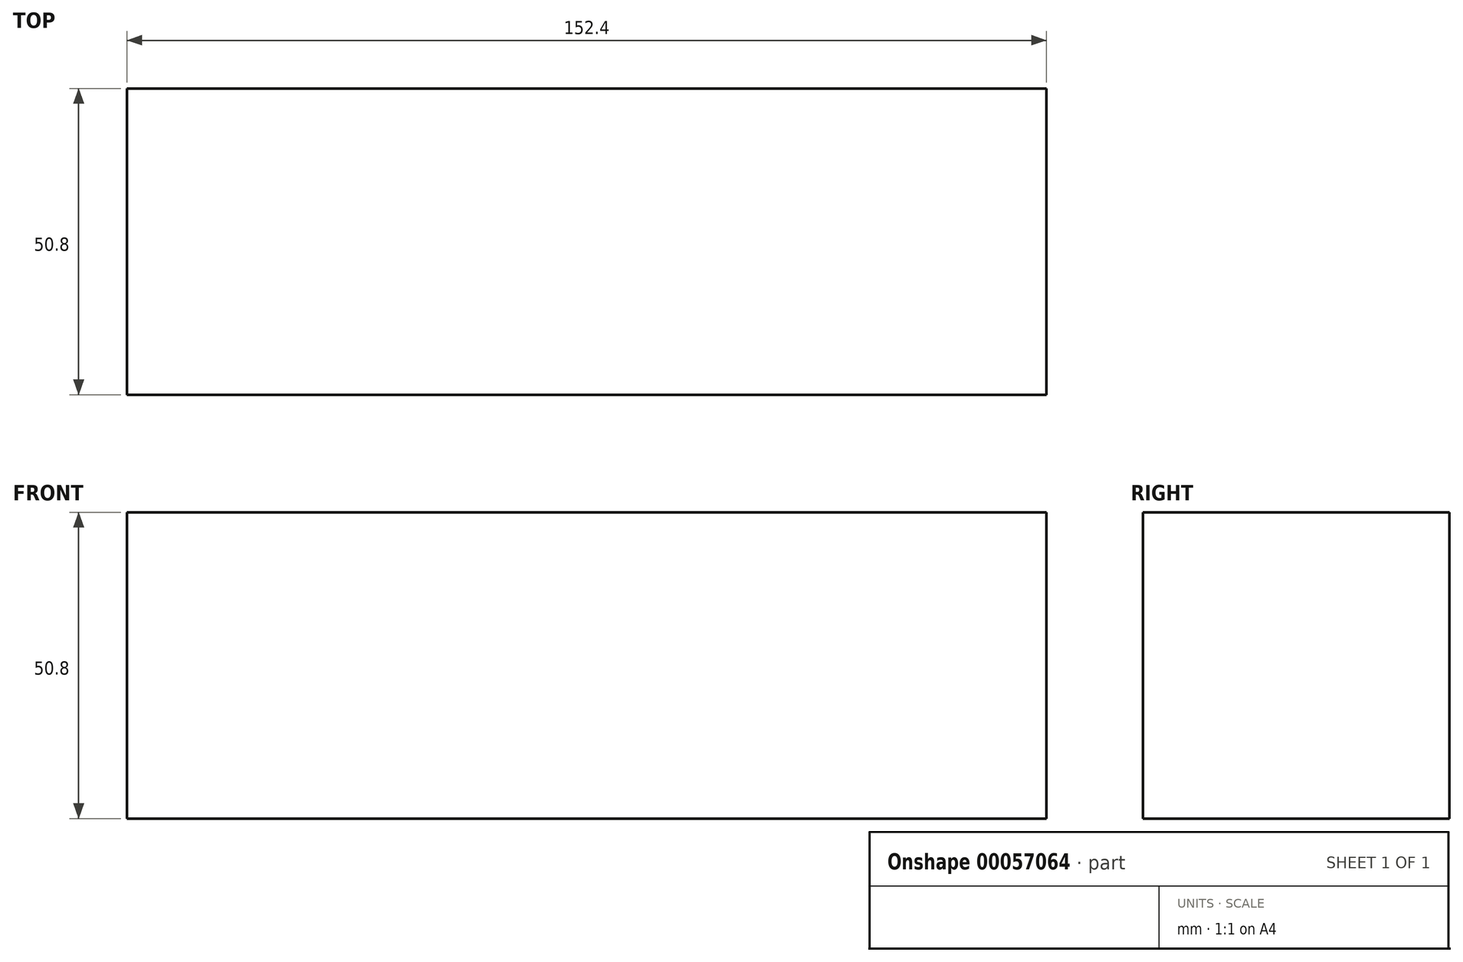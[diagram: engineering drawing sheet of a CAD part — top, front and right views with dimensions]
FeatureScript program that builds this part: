
annotation { "Feature Type Name" : "Feature", "Feature Type Description" : "" }
export const myFeature = defineFeature(function(context is Context, id is Id, definition is map)
    precondition{}
    {
        {
            var Q0;
            Q0=qCreatedBy(makeId("Front.planeOp"),FACE);
            var sketch = newSketch(context, id + "F0", { "sketchPlane" : qUnion([Q0])});
            skLineSegment(sketch, "E0.bottom", {"start": v(-50.8, -43) * mm, "end": v(101.6, -43) * mm});
            skLineSegment(sketch, "E0.top", {"start": v(-50.8, 7.8) * mm, "end": v(101.6, 7.8) * mm});
            skLineSegment(sketch, "E0.left", {"start": v(-50.8, -43) * mm, "end": v(-50.8, 7.8) * mm});
            skLineSegment(sketch, "E0.right", {"start": v(101.6, -43) * mm, "end": v(101.6, 7.8) * mm});
            skLineSegment(sketch, "E1.bottom", {"start": v(-50.8, 7.8) * mm, "end": v(0, 7.8) * mm});
            skLineSegment(sketch, "E1.top", {"start": v(-50.8, 84) * mm, "end": v(0, 84) * mm});
            skLineSegment(sketch, "E1.left", {"start": v(-50.8, 7.8) * mm, "end": v(-50.8, 84) * mm});
            skLineSegment(sketch, "E1.right", {"start": v(0, 7.8) * mm, "end": v(0, 84) * mm});
            skSolve(sketch);
        }
        {
            var Q0;
            Q0=makeQuery(id+"F0.imprint","IMPRINT",FACE,{"disambiguationData":[TD([[makeQuery(id+"F0.imprint","IMPRINT",EDGE,{"derivedFrom":sQuery(id+"F0.wireOp",EDGE,"E0.bottom")}),1.0]])]});
            var Q1;
            Q1=makeQuery(id+"F0.imprint","IMPRINT",FACE,{"disambiguationData":[TD([[makeQuery(id+"F0.imprint","IMPRINT",EDGE,{"derivedFrom":sQuery(id+"F0.wireOp",EDGE,"E1.bottom")}),1.0]])]});
            extrude(context, id + "F1", {"entities" : qUnion([Q0, Q1]), "depth" : 50.8 * mm});
        }
    });
